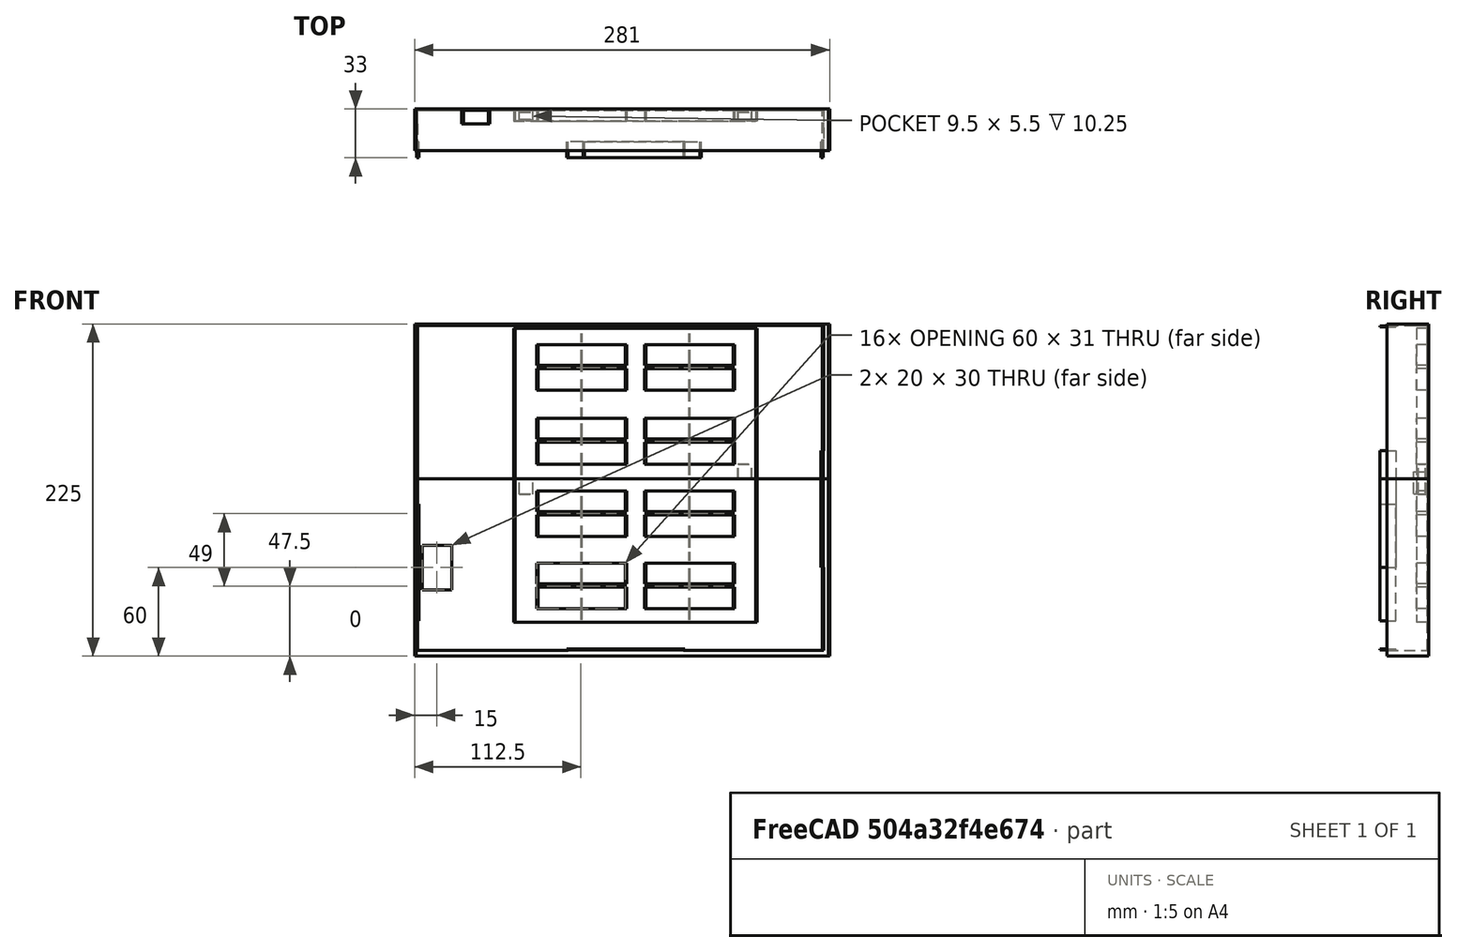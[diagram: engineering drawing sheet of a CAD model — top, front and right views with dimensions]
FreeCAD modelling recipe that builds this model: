
FCSTD DOCUMENT  (FreeCAD 0.19R24291 (Git))
Label: estructura_superior
License: All rights reserved
LicenseURL: http://en.wikipedia.org/wiki/All_rights_reserved
objects: Part::Box×19, Part::Cut×9, Part::Feature×8, Part::MultiFuse×6
note: 42 computed .brp shape members not serialized (recipe doc carries the construction recipe); baked Part::Feature solids carry a one-line shape summary decoded from their .brp

FEATURE [Part::Box] Box  label="Cubo"
  AttacherType = Attacher::AttachEngine3D
  Height = 275
  Length = 1
  Placement = pos=(-50,40,-147) rot=(0,0,1;0rad)
  Width = 28
FEATURE [Part::Box] Box001  label="Cubo001"
  AttacherType = Attacher::AttachEngine3D
  Height = 275
  Length = 4
  Placement = pos=(171,40,-147) rot=(0,0,1;0rad)
  Width = 28
FEATURE [Part::Box] Box002  label="Cubo002"
  AttacherType = Attacher::AttachEngine3D
  Height = 18
  Length = 1
  Placement = pos=(-50,58,-116) rot=(0,0,1;0rad)
  Width = 10
FEATURE [Part::Box] Box003  label="Cubo003"
  AttacherType = Attacher::AttachEngine3D
  Height = 1
  Length = 225
  Placement = pos=(-50,40,-148) rot=(0,0,1;0rad)
  Width = 28
FEATURE [Part::Box] Box004  label="Cubo004"
  AttacherType = Attacher::AttachEngine3D
  Height = 4
  Length = 225
  Placement = pos=(-50,40,128) rot=(0,0,1;0rad)
  Width = 28
FEATURE [Part::Box] Box041  label="Cubo041"
  AttacherType = Attacher::AttachEngine3D
  Height = 10
  Length = 15
  Placement = pos=(50,58,-149) rot=(0,0,1;0rad)
  Width = 10
FEATURE [Part::Feature] Fusion003_solid  label="estructuraTope (Solid)001"
  Placement = pos=(151,48,2) rot=(1,0,0;1.5708rad)
  shape: bbox 199 x 4 x 164 mm, 86 faces (baked)
FEATURE [Part::Feature] Fusion003_solid001  label="estructuraTope (Solid)002"
  Placement = pos=(151,52,2) rot=(1,0,0;1.5708rad)
  shape: bbox 199 x 4 x 164 mm, 86 faces (baked)
FEATURE [Part::MultiFuse] Fusion011
  Placement = pos=(-1,0,-2) rot=(0,0,1;0rad)
  Shapes = -> [Fusion003_solid001,Fusion003_solid]
FEATURE [Part::Cut] Cut001
  Base = -> Box003
  Tool = -> Box041
FEATURE [Part::Cut] Cut
  Base = -> Box
  Tool = -> Box002
FEATURE [Part::Box] Box042  label="Cubo042"
  AttacherType = Attacher::AttachEngine3D
  Height = 82
  Length = 222
  Placement = pos=(-50,67,-148) rot=(0,0,1;0rad)
  Width = 1
FEATURE [Part::Box] Box043  label="Cubo043"
  AttacherType = Attacher::AttachEngine3D
  Height = 62
  Length = 222
  Placement = pos=(-49,67,68) rot=(0,0,1;0rad)
  Width = 1
FEATURE [Part::Box] Box044  label="Cubo044"
  AttacherType = Attacher::AttachEngine3D
  Height = 200
  Length = 10
  Placement = pos=(-49,67,-70) rot=(0,0,1;0rad)
  Width = 1
FEATURE [Part::Box] Box045  label="Cubo045"
  AttacherType = Attacher::AttachEngine3D
  Height = 200
  Length = 20
  Placement = pos=(152,67,-79) rot=(0,0,1;0rad)
  Width = 1
FEATURE [Part::MultiFuse] Fusion012
  Shapes = -> [Cut,Cut001,Box004,Box001,Box042,Box043,Box044,Box045]
FEATURE [Part::MultiFuse] Fusion013
  Shapes = -> [Fusion012,Fusion011]
FEATURE [Part::Box] Box046  label="Cubo046"
  AttacherType = Attacher::AttachEngine3D
  Height = 79
  Length = 1
  Placement = pos=(-49,35,-34) rot=(0,0,1;0rad)
  Width = 11
FEATURE [Part::Box] Box047  label="Cubo047"
  AttacherType = Attacher::AttachEngine3D
  Height = 79
  Length = 0.25
  Placement = pos=(-49,35,-34) rot=(0,0,1;0rad)
  Width = 5
FEATURE [Part::Cut] Cut002
  Base = -> Box046
  Tool = -> Box047
FEATURE [Part::Feature] Cut002_solid  label="Cut002 (Solid)"
  Placement = pos=(122,0,0) rot=(0,1,0;3.14159rad)
  shape: bbox 1 x 11 x 79 mm, 8 faces (baked)
FEATURE [Part::Feature] Cut002_solid001  label="Cut002 (Solid)001"
  Placement = pos=(70,0,79) rot=(0,1,0;1.5708rad)
  shape: bbox 79 x 11 x 1 mm, 8 faces (baked)
FEATURE [Part::Feature] Cut002_solid002  label="Cut002 (Solid)002"
  Placement = pos=(117,0,-98) rot=(0,-1,0;1.5708rad)
  shape: bbox 79 x 11 x 1 mm, 8 faces (baked)
FEATURE [Part::MultiFuse] Fusion014  label="estructura_SuperiorCompleta"
  Placement = pos=(83,-2,-26) rot=(0,1,0;1.5708rad)
  Shapes = -> [Cut002,Fusion013,Cut002_solid,Cut002_solid001,Cut002_solid002]
FEATURE [Part::Feature] Fusion014_solid  label="estructura_SuperiorCompleta (Solid)"
  Placement = pos=(84,-2,-26) rot=(0,1,0;1.5708rad)
  shape: bbox 280 x 33 x 225 mm, 247 faces (baked)
FEATURE [Part::Box] Box048  label="Cubo048"
  AttacherType = Attacher::AttachEngine3D
  Height = 1000
  Length = 1000
  Placement = pos=(-80,23,-1081) rot=(0,0,1;0rad)
  Width = 1000
FEATURE [Part::Cut] Cut003
  Base = -> Fusion014_solid
  Tool = -> Box048
FEATURE [Part::Feature] Fusion014_solid001  label="estructura_SuperiorCompleta (Solid)001"
  Placement = pos=(84,-2,-26) rot=(0,1,0;1.5708rad)
  shape: bbox 280 x 33 x 225 mm, 247 faces (baked)
FEATURE [Part::Feature] Cut003_solid  label="Cut003 (Solid)"
  shape: bbox 280 x 33 x 105 mm, 139 faces (baked)
FEATURE [Part::Cut] Cut004
  Base = -> Fusion014_solid001
  Placement = pos=(0,0,-15) rot=(0,0,1;0rad)
  Tool = -> Cut003_solid
FEATURE [Part::Box] Box049  label="Cubo049"
  AttacherType = Attacher::AttachEngine3D
  Height = 10
  Length = 9
  Placement = pos=(6,59,-91) rot=(0,0,1;0rad)
  Width = 5
FEATURE [Part::Box] Box050  label="Cubo050"
  AttacherType = Attacher::AttachEngine3D
  Height = 10
  Length = 9
  Placement = pos=(154,59,-96) rot=(0,0,1;0rad)
  Width = 5
FEATURE [Part::Box] Box051  label="Cubo051"
  AttacherType = Attacher::AttachEngine3D
  Height = 10.25
  Length = 9.5
  Placement = pos=(5.75,58.75,-106.25) rot=(0,0,1;0rad)
  Width = 5.5
FEATURE [Part::Cut] Cut005
  Base = -> Cut004
  Tool = -> Box051
FEATURE [Part::Box] Box052  label="Cubo052"
  AttacherType = Attacher::AttachEngine3D
  Height = 10.25
  Length = 9.5
  Placement = pos=(153.75,58.75,-81) rot=(0,0,1;0rad)
  Width = 5.5
FEATURE [Part::Cut] Cut006
  Base = -> Cut003
  Tool = -> Box052
FEATURE [Part::MultiFuse] Fusion015  label="EstructuraCompleta1"
  Placement = pos=(0,0,15) rot=(0,0,1;0rad)
  Shapes = -> [Cut005,Box050]
FEATURE [Part::MultiFuse] Fusion016  label="EstructuraSuperiorCompleta2"
  Shapes = -> [Cut006,Box049]
FEATURE [Part::Box] Box053  label="Cubo053"
  AttacherType = Attacher::AttachEngine3D
  Height = 30
  Length = 20
  Placement = pos=(-60,51,-156) rot=(0,0,1;0rad)
  Width = 22
FEATURE [Part::Box] Box054  label="Cubo054"
  AttacherType = Attacher::AttachEngine3D
  Height = 30
  Length = 20
  Placement = pos=(-60,51,-156) rot=(0,0,1;0rad)
  Width = 22
FEATURE [Part::Cut] Cut007  label="estructuraSuperiorCompleta"
  Base = -> Fusion014
  Tool = -> Box053
FEATURE [Part::Cut] Cut008  label="estructuraSuperiorCompleta1"
  Base = -> Fusion015
  Tool = -> Box054
